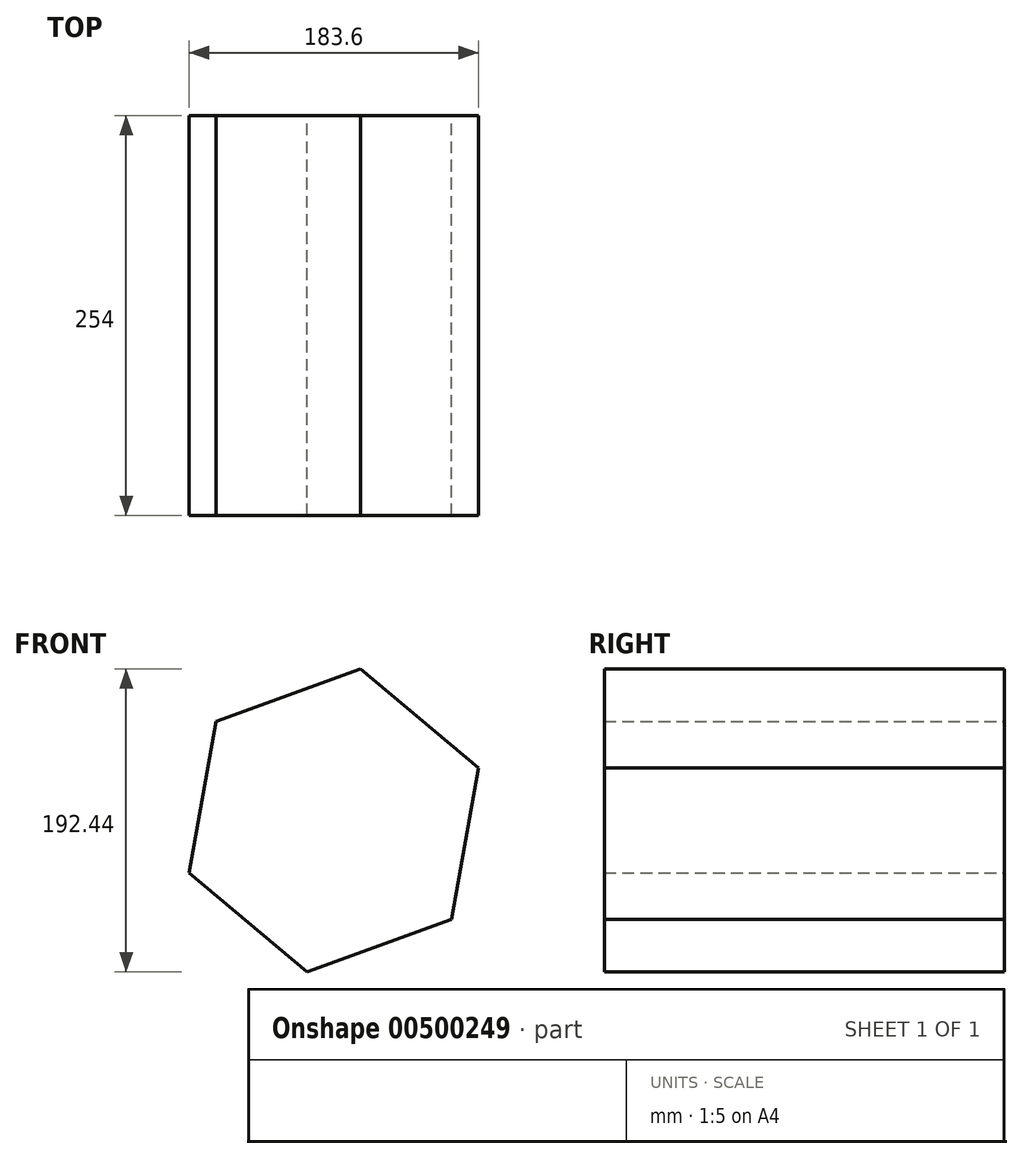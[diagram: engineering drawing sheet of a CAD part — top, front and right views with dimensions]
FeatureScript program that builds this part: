
annotation { "Feature Type Name" : "Feature", "Feature Type Description" : "" }
export const myFeature = defineFeature(function(context is Context, id is Id, definition is map)
    precondition{}
    {
        {
            var Q0;
            Q0=qCreatedBy(makeId("Front.planeOp"),FACE);
            var sketch = newSketch(context, id + "F0", { "sketchPlane" : qUnion([Q0])});
            skCircle(sketch, "E0.cCircle", {"center": v(0, 0) * mm, "radius": 97.7 * mm, "construction": true});
            skLineSegment(sketch, "E0.0", {"start": v(-91.8, -33.42) * mm, "end": v(-74.85, 62.8) * mm});
            skLineSegment(sketch, "E0.1", {"start": v(-74.85, 62.8) * mm, "end": v(16.96, 96.22) * mm});
            skLineSegment(sketch, "E0.2", {"start": v(16.96, 96.22) * mm, "end": v(91.8, 33.42) * mm});
            skLineSegment(sketch, "E0.3", {"start": v(91.8, 33.42) * mm, "end": v(74.85, -62.8) * mm});
            skLineSegment(sketch, "E0.4", {"start": v(74.85, -62.8) * mm, "end": v(-16.96, -96.22) * mm});
            skLineSegment(sketch, "E0.5", {"start": v(-16.96, -96.22) * mm, "end": v(-91.8, -33.42) * mm});
            skSolve(sketch);
        }
        {
            var Q0;
            Q0=makeQuery(id+"F0.imprint","IMPRINT",FACE,{"disambiguationData":[TD([[makeQuery(id+"F0.imprint","IMPRINT",EDGE,{"derivedFrom":sQuery(id+"F0.wireOp",EDGE,"E0.0")}),-1.0]])]});
            extrude(context, id + "F1", {"entities" : qUnion([Q0]), "depth" : 254 * mm, "offsetDistance" : 25 * mm});
        }
    });
